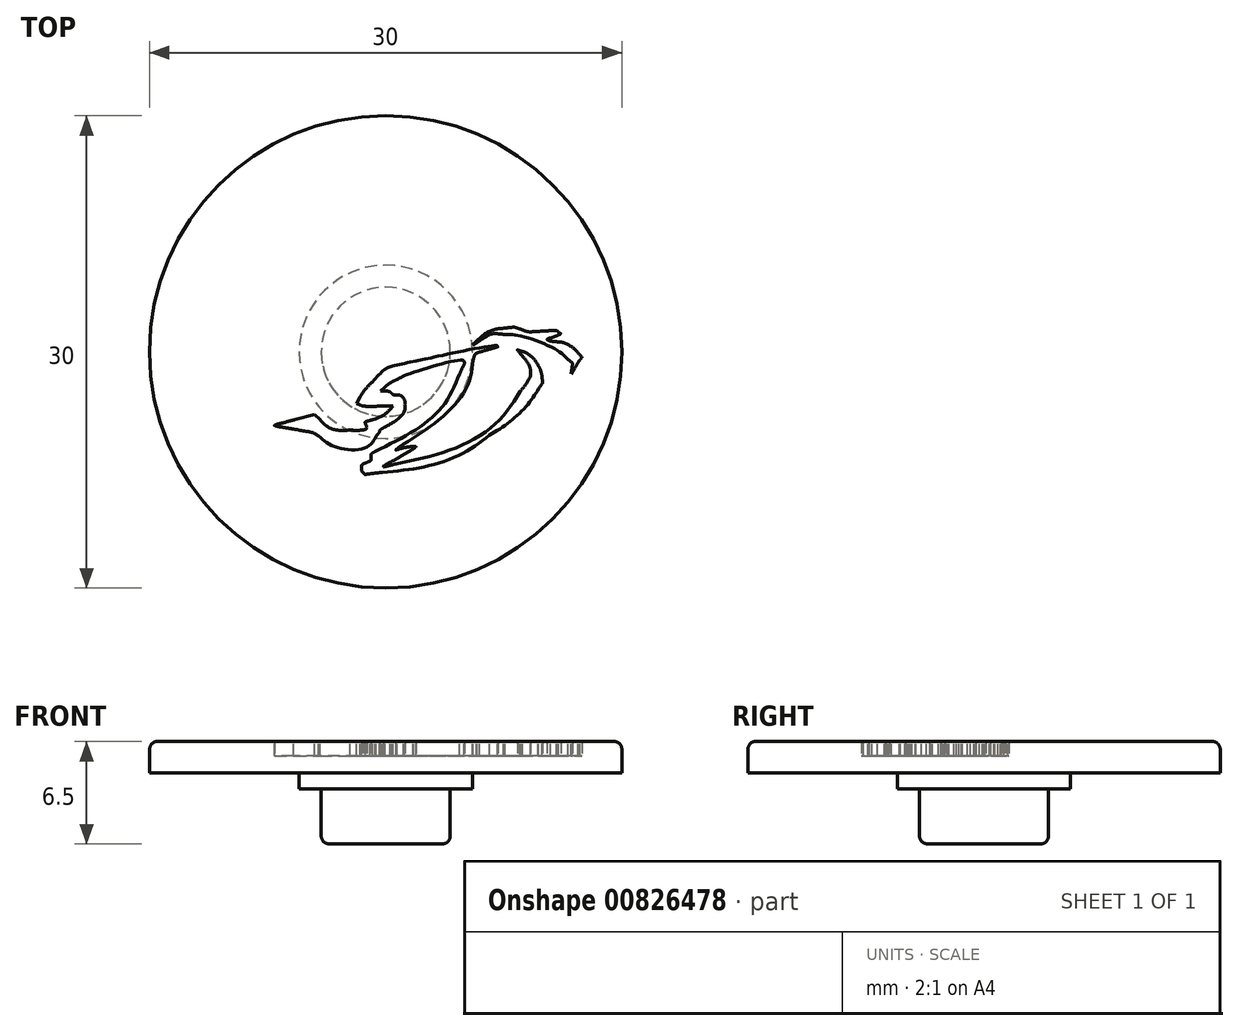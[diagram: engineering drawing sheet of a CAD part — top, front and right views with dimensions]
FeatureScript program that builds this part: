
annotation { "Feature Type Name" : "Feature", "Feature Type Description" : "" }
export const myFeature = defineFeature(function(context is Context, id is Id, definition is map)
    precondition{}
    {
        {
            var Q0;
            Q0=qCreatedBy(makeId("Top.planeOp"),FACE);
            var sketch = newSketch(context, id + "F0", { "sketchPlane" : qUnion([Q0])});
            skFitSpline(sketch, "E0", {"points": [v(-1.44, -7.67) * mm, v(-1.49, -7.62) * mm, v(-1.53, -7.5) * mm, v(-1.53, -7.38) * mm]});
            skFitSpline(sketch, "E1", {"points": [v(-1.53, -7.38) * mm, v(-1.53, -7.2) * mm, v(-1.47, -7.14) * mm, v(-1.23, -7.03) * mm]});
            skFitSpline(sketch, "E2", {"points": [v(-1.23, -7.03) * mm, v(-0.97, -6.92) * mm, v(-0.92, -6.86) * mm, v(-0.92, -6.68) * mm]});
            skFitSpline(sketch, "E3", {"points": [v(-0.92, -6.68) * mm, v(-0.92, -6.52) * mm, v(-0.87, -6.44) * mm, v(-0.68, -6.34) * mm]});
            skFitSpline(sketch, "E4", {"points": [v(-0.68, -6.34) * mm, v(2.05, -4.85) * mm, v(3.75, -3.29) * mm, v(4.68, -1.4) * mm]});
            skFitSpline(sketch, "E5", {"points": [v(4.68, -1.4) * mm, v(4.88, -1.01) * mm, v(5.01, -0.68) * mm, v(4.99, -0.65) * mm]});
            skFitSpline(sketch, "E6", {"points": [v(4.99, -0.65) * mm, v(4.87, -0.53) * mm, v(1.46, -1.41) * mm, v(0.72, -1.76) * mm]});
            skFitSpline(sketch, "E7", {"points": [v(0.72, -1.76) * mm, v(0.46, -1.87) * mm, v(0.12, -2.09) * mm, v(-0.04, -2.23) * mm]});
            skFitSpline(sketch, "E8", {"points": [v(-0.06, -2.5) * mm, v(0.09, -2.5) * mm, v(0.27, -2.55) * mm, v(0.35, -2.62) * mm]});
            skFitSpline(sketch, "E9", {"points": [v(0.35, -2.62) * mm, v(0.43, -2.7) * mm, v(0.57, -2.75) * mm, v(0.66, -2.75) * mm]});
            skFitSpline(sketch, "E10", {"points": [v(0.66, -2.75) * mm, v(0.9, -2.75) * mm, v(1.2, -3.08) * mm, v(1.2, -3.34) * mm]});
            skFitSpline(sketch, "E11", {"points": [v(1.2, -3.34) * mm, v(1.2, -3.73) * mm, v(0.66, -4.35) * mm, v(-0.06, -4.77) * mm]});
            skFitSpline(sketch, "E12", {"points": [v(-0.06, -4.77) * mm, v(-0.24, -4.88) * mm, v(-0.4, -5) * mm, v(-0.4, -5.03) * mm]});
            skFitSpline(sketch, "E13", {"points": [v(-0.4, -5.03) * mm, v(-0.4, -5.07) * mm, v(-0.5, -5.22) * mm, v(-0.62, -5.36) * mm]});
            skFitSpline(sketch, "E14", {"points": [v(-0.62, -5.36) * mm, v(-1.25, -6.07) * mm, v(-3.14, -6.06) * mm, v(-4.28, -5.34) * mm]});
            skFitSpline(sketch, "E15", {"points": [v(-4.28, -5.34) * mm, v(-4.56, -5.16) * mm, v(-4.85, -5.08) * mm, v(-5.85, -4.91) * mm]});
            skFitSpline(sketch, "E16", {"points": [v(-5.85, -4.91) * mm, v(-6.53, -4.8) * mm, v(-7.06, -4.68) * mm, v(-7.05, -4.67) * mm]});
            skFitSpline(sketch, "E17", {"points": [v(-7.05, -4.67) * mm, v(-7.03, -4.65) * mm, v(-6.46, -4.5) * mm, v(-5.77, -4.31) * mm]});
            skLineSegment(sketch, "E18", {"start": v(-0.04, -2.23) * mm, "end": v(-0.34, -2.5) * mm});
            skLineSegment(sketch, "E19", {"start": v(-0.34, -2.5) * mm, "end": v(-0.06, -2.5) * mm});
            skFitSpline(sketch, "E20", {"points": [v(-4.17, -4.31) * mm, v(-3.65, -4.78) * mm, v(-3.1, -4.97) * mm, v(-2.27, -4.97) * mm]});
            skFitSpline(sketch, "E21", {"points": [v(-2.27, -4.97) * mm, v(-1.54, -4.97) * mm, v(-1.2, -4.85) * mm, v(-1.28, -4.59) * mm]});
            skFitSpline(sketch, "E22", {"points": [v(-1.28, -4.59) * mm, v(-1.3, -4.48) * mm, v(-1.25, -4.43) * mm, v(-0.98, -4.35) * mm]});
            skFitSpline(sketch, "E23", {"points": [v(-0.98, -4.35) * mm, v(-0.53, -4.22) * mm, v(0.01, -3.91) * mm, v(0.26, -3.66) * mm]});
            skLineSegment(sketch, "E24", {"start": v(-5.77, -4.31) * mm, "end": v(-4.53, -3.99) * mm});
            skLineSegment(sketch, "E25", {"start": v(-4.53, -3.99) * mm, "end": v(-4.17, -4.31) * mm});
            skFitSpline(sketch, "E26", {"points": [v(-0.48, -3.46) * mm, v(-1.07, -3.46) * mm, v(-1.5, -3.43) * mm, v(-1.63, -3.37) * mm]});
            skLineSegment(sketch, "E27", {"start": v(0.26, -3.66) * mm, "end": v(0.46, -3.44) * mm});
            skLineSegment(sketch, "E28", {"start": v(0.46, -3.44) * mm, "end": v(-0.48, -3.46) * mm});
            skFitSpline(sketch, "E29", {"points": [v(-1.63, -2.88) * mm, v(-1.51, -2.66) * mm, v(-1.16, -2.22) * mm, v(-0.85, -1.9) * mm]});
            skFitSpline(sketch, "E30", {"points": [v(-0.85, -1.9) * mm, v(-0.09, -1.14) * mm, v(0.37, -0.92) * mm, v(1.93, -0.58) * mm]});
            skFitSpline(sketch, "E31", {"points": [v(1.93, -0.58) * mm, v(3.42, -0.26) * mm, v(7.06, 0.4) * mm, v(7.1, 0.35) * mm]});
            skFitSpline(sketch, "E32", {"points": [v(7.1, 0.35) * mm, v(7.12, 0.33) * mm, v(6.86, 0.23) * mm, v(6.5, 0.14) * mm]});
            skFitSpline(sketch, "E33", {"points": [v(6.5, 0.14) * mm, v(6.16, 0.04) * mm, v(5.83, -0.06) * mm, v(5.76, -0.1) * mm]});
            skFitSpline(sketch, "E34", {"points": [v(5.76, -0.1) * mm, v(5.7, -0.13) * mm, v(5.6, -0.34) * mm, v(5.55, -0.56) * mm]});
            skFitSpline(sketch, "E35", {"points": [v(5.55, -0.56) * mm, v(5.17, -2.2) * mm, v(3.48, -4.23) * mm, v(1.13, -5.87) * mm]});
            skFitSpline(sketch, "E36", {"points": [v(1.13, -5.87) * mm, v(0.82, -6.08) * mm, v(0.63, -6.24) * mm, v(0.71, -6.22) * mm]});
            skFitSpline(sketch, "E37", {"points": [v(0.71, -6.22) * mm, v(1.08, -6.11) * mm, v(1.56, -6.02) * mm, v(1.74, -6.02) * mm]});
            skFitSpline(sketch, "E38", {"points": [v(1.74, -6.02) * mm, v(1.92, -6.02) * mm, v(1.92, -6.02) * mm, v(1.78, -6.14) * mm]});
            skFitSpline(sketch, "E39", {"points": [v(1.78, -6.14) * mm, v(1.7, -6.2) * mm, v(1.22, -6.48) * mm, v(0.73, -6.76) * mm]});
            skFitSpline(sketch, "E40", {"points": [v(0.73, -6.76) * mm, v(0.24, -7.04) * mm, v(-0.15, -7.27) * mm, v(-0.13, -7.29) * mm]});
            skFitSpline(sketch, "E41", {"points": [v(-0.13, -7.29) * mm, v(-0.12, -7.3) * mm, v(0.23, -7.22) * mm, v(0.64, -7.12) * mm]});
            skFitSpline(sketch, "E42", {"points": [v(0.64, -7.12) * mm, v(4.15, -6.21) * mm, v(6.96, -4.58) * mm, v(8.53, -2.53) * mm]});
            skFitSpline(sketch, "E43", {"points": [v(8.53, -2.53) * mm, v(8.88, -2.08) * mm, v(9.19, -1.53) * mm, v(9.19, -1.36) * mm]});
            skFitSpline(sketch, "E44", {"points": [v(9.19, -1.36) * mm, v(9.19, -1.08) * mm, v(8.99, -0.65) * mm, v(8.7, -0.28) * mm]});
            skFitSpline(sketch, "E45", {"points": [v(8.7, -0.28) * mm, v(8.38, 0.1) * mm, v(8.37, 0.12) * mm, v(8.56, 0.06) * mm]});
            skFitSpline(sketch, "E46", {"points": [v(8.56, 0.06) * mm, v(8.93, -0.08) * mm, v(9.48, -0.53) * mm, v(9.68, -0.88) * mm]});
            skFitSpline(sketch, "E47", {"points": [v(9.68, -0.88) * mm, v(9.79, -1.06) * mm, v(9.9, -1.38) * mm, v(9.92, -1.6) * mm]});
            skFitSpline(sketch, "E48", {"points": [v(9.92, -1.6) * mm, v(9.96, -1.93) * mm, v(9.94, -2) * mm, v(9.72, -2.33) * mm]});
            skFitSpline(sketch, "E49", {"points": [v(9.72, -2.33) * mm, v(9.03, -3.34) * mm, v(7.85, -4.46) * mm, v(6.6, -5.3) * mm]});
            skFitSpline(sketch, "E50", {"points": [v(6.6, -5.3) * mm, v(4.85, -6.47) * mm, v(2.43, -7.3) * mm, v(-0.2, -7.65) * mm]});
            skFitSpline(sketch, "E51", {"points": [v(-0.2, -7.65) * mm, v(-1.29, -7.79) * mm, v(-1.32, -7.8) * mm, v(-1.44, -7.67) * mm]});
            skLineSegment(sketch, "E52", {"start": v(-1.63, -3.37) * mm, "end": v(-1.84, -3.28) * mm});
            skLineSegment(sketch, "E53", {"start": v(-1.84, -3.28) * mm, "end": v(-1.63, -2.88) * mm});
            skFitSpline(sketch, "E54", {"points": [v(-7.59, -3.23) * mm, v(-7.06, -2.2) * mm, v(-7.01, -1.09) * mm, v(-7.46, -0.25) * mm]});
            skFitSpline(sketch, "E55", {"points": [v(-7.46, -0.25) * mm, v(-8.22, 1.18) * mm, v(-9.95, 2.18) * mm, v(-13.43, 3.2) * mm]});
            skFitSpline(sketch, "E56", {"points": [v(-13.43, 3.2) * mm, v(-13.8, 3.31) * mm, v(-13.74, 3.32) * mm, v(-12.25, 3.32) * mm]});
            skFitSpline(sketch, "E57", {"points": [v(-12.25, 3.32) * mm, v(-10.97, 3.32) * mm, v(-10.56, 3.35) * mm, v(-9.94, 3.48) * mm]});
            skFitSpline(sketch, "E58", {"points": [v(-9.94, 3.48) * mm, v(-8.94, 3.69) * mm, v(-8.97, 3.7) * mm, v(-9.13, 3.35) * mm]});
            skFitSpline(sketch, "E59", {"points": [v(-9.13, 3.35) * mm, v(-9.4, 2.79) * mm, v(-9.4, 2.77) * mm, v(-8.95, 2.55) * mm]});
            skLineSegment(sketch, "E60", {"start": v(-1.44, -7.67) * mm, "end": v(-1.44, -7.67) * mm});
            skFitSpline(sketch, "E61", {"points": [v(-8.2, 2.8) * mm, v(-7.9, 3.18) * mm, v(-7.03, 3.86) * mm, v(-6.84, 3.86) * mm]});
            skFitSpline(sketch, "E62", {"points": [v(-6.84, 3.86) * mm, v(-6.72, 3.86) * mm, v(-6.78, 3.7) * mm, v(-7, 3.4) * mm]});
            skFitSpline(sketch, "E63", {"points": [v(-7, 3.4) * mm, v(-7.22, 3.13) * mm, v(-7.63, 2.32) * mm, v(-7.71, 2) * mm]});
            skFitSpline(sketch, "E64", {"points": [v(-7.71, 2) * mm, v(-7.74, 1.89) * mm, v(-7.66, 1.77) * mm, v(-7.36, 1.54) * mm]});
            skLineSegment(sketch, "E65", {"start": v(-8.95, 2.55) * mm, "end": v(-8.54, 2.35) * mm});
            skLineSegment(sketch, "E66", {"start": v(-8.54, 2.35) * mm, "end": v(-8.2, 2.8) * mm});
            skFitSpline(sketch, "E67", {"points": [v(-6.78, 1.63) * mm, v(-6.69, 1.86) * mm, v(-6.48, 2.2) * mm, v(-6.34, 2.38) * mm]});
            skFitSpline(sketch, "E68", {"points": [v(-6.34, 2.38) * mm, v(-6.08, 2.71) * mm, v(-5.24, 3.4) * mm, v(-5.1, 3.4) * mm]});
            skFitSpline(sketch, "E69", {"points": [v(-5.1, 3.4) * mm, v(-4.95, 3.4) * mm, v(-5.04, 3.16) * mm, v(-5.35, 2.7) * mm]});
            skFitSpline(sketch, "E70", {"points": [v(-5.35, 2.7) * mm, v(-5.83, 2) * mm, v(-6.01, 1.37) * mm, v(-6.1, 0.1) * mm]});
            skFitSpline(sketch, "E71", {"points": [v(-6.1, 0.1) * mm, v(-6.17, -1.02) * mm, v(-6.3, -1.64) * mm, v(-6.56, -2.16) * mm]});
            skFitSpline(sketch, "E72", {"points": [v(-6.56, -2.16) * mm, v(-6.79, -2.62) * mm, v(-7.26, -3.24) * mm, v(-7.54, -3.44) * mm]});
            skLineSegment(sketch, "E73", {"start": v(-7.36, 1.54) * mm, "end": v(-6.96, 1.23) * mm});
            skLineSegment(sketch, "E74", {"start": v(-6.96, 1.23) * mm, "end": v(-6.78, 1.63) * mm});
            skFitSpline(sketch, "E75", {"points": [v(-4.41, -2.77) * mm, v(-4.42, -2.13) * mm, v(-4.2, -1.56) * mm, v(-3.73, -1.05) * mm]});
            skFitSpline(sketch, "E76", {"points": [v(-3.73, -1.05) * mm, v(-3.53, -0.83) * mm, v(-3.2, -0.56) * mm, v(-3.01, -0.46) * mm]});
            skFitSpline(sketch, "E77", {"points": [v(-3.01, -0.46) * mm, v(-2.71, -0.3) * mm, v(-2.65, -0.23) * mm, v(-2.55, 0.1) * mm]});
            skFitSpline(sketch, "E78", {"points": [v(-2.55, 0.1) * mm, v(-2.43, 0.52) * mm, v(-2.41, 0.89) * mm, v(-2.51, 1.04) * mm]});
            skFitSpline(sketch, "E79", {"points": [v(-2.51, 1.04) * mm, v(-2.61, 1.2) * mm, v(-3.05, 1.11) * mm, v(-3.83, 0.79) * mm]});
            skFitSpline(sketch, "E80", {"points": [v(-3.83, 0.79) * mm, v(-5.04, 0.27) * mm, v(-5.33, -0.03) * mm, v(-5.33, -0.8) * mm]});
            skFitSpline(sketch, "E81", {"points": [v(-5.33, -0.8) * mm, v(-5.33, -1.06) * mm, v(-5.3, -1.4) * mm, v(-5.26, -1.55) * mm]});
            skFitSpline(sketch, "E82", {"points": [v(-5.26, -1.55) * mm, v(-5.23, -1.7) * mm, v(-5.22, -1.82) * mm, v(-5.25, -1.8) * mm]});
            skFitSpline(sketch, "E83", {"points": [v(-5.25, -1.8) * mm, v(-5.38, -1.72) * mm, v(-5.5, -0.74) * mm, v(-5.46, -0.1) * mm]});
            skFitSpline(sketch, "E84", {"points": [v(-5.46, -0.1) * mm, v(-5.42, 0.63) * mm, v(-5.22, 1.25) * mm, v(-4.84, 1.83) * mm]});
            skLineSegment(sketch, "E85", {"start": v(-7.54, -3.44) * mm, "end": v(-7.78, -3.6) * mm});
            skLineSegment(sketch, "E86", {"start": v(-7.78, -3.6) * mm, "end": v(-7.59, -3.23) * mm});
            skFitSpline(sketch, "E87", {"points": [v(-2.15, 2.2) * mm, v(0.25, 2.2) * mm, v(0.32, 2.2) * mm, v(0.59, 2.36) * mm]});
            skFitSpline(sketch, "E88", {"points": [v(0.59, 2.36) * mm, v(1.61, 2.98) * mm, v(2.34, 3.8) * mm, v(2.5, 4.5) * mm]});
            skFitSpline(sketch, "E89", {"points": [v(2.5, 4.5) * mm, v(2.59, 4.88) * mm, v(2.52, 5.38) * mm, v(2.32, 5.85) * mm]});
            skFitSpline(sketch, "E90", {"points": [v(2.32, 5.85) * mm, v(2.27, 5.95) * mm, v(2.37, 5.98) * mm, v(3.05, 6.02) * mm]});
            skFitSpline(sketch, "E91", {"points": [v(3.05, 6.02) * mm, v(3.48, 6.05) * mm, v(4, 6.1) * mm, v(4.2, 6.11) * mm]});
            skLineSegment(sketch, "E92", {"start": v(-4.84, 1.83) * mm, "end": v(-4.6, 2.19) * mm});
            skLineSegment(sketch, "E93", {"start": v(-4.6, 2.19) * mm, "end": v(-2.15, 2.2) * mm});
            skFitSpline(sketch, "E94", {"points": [v(4.36, 6.03) * mm, v(4.02, 5.84) * mm, v(3.57, 5.38) * mm, v(3.39, 5.04) * mm]});
            skFitSpline(sketch, "E95", {"points": [v(3.39, 5.04) * mm, v(3.25, 4.8) * mm, v(3.22, 4.61) * mm, v(3.22, 4.05) * mm]});
            skFitSpline(sketch, "E96", {"points": [v(3.22, 4.05) * mm, v(3.22, 3.33) * mm, v(3.29, 3.13) * mm, v(3.69, 2.6) * mm]});
            skLineSegment(sketch, "E97", {"start": v(4.2, 6.11) * mm, "end": v(4.59, 6.15) * mm});
            skLineSegment(sketch, "E98", {"start": v(4.59, 6.15) * mm, "end": v(4.36, 6.03) * mm});
            skFitSpline(sketch, "E99", {"points": [v(9.16, 2.14) * mm, v(9.58, 1.94) * mm, v(10.16, 1.87) * mm, v(10.58, 1.99) * mm]});
            skLineSegment(sketch, "E100", {"start": v(3.69, 2.6) * mm, "end": v(3.87, 2.34) * mm});
            skLineSegment(sketch, "E101", {"start": v(3.87, 2.34) * mm, "end": v(6.31, 2.34) * mm});
            skLineSegment(sketch, "E102", {"start": v(6.31, 2.34) * mm, "end": v(8.75, 2.34) * mm});
            skLineSegment(sketch, "E103", {"start": v(8.75, 2.34) * mm, "end": v(9.16, 2.14) * mm});
            skFitSpline(sketch, "E104", {"points": [v(10.27, 2.6) * mm, v(9.76, 3.16) * mm, v(9.5, 3.57) * mm, v(9.5, 3.82) * mm]});
            skFitSpline(sketch, "E105", {"points": [v(9.5, 3.82) * mm, v(9.5, 4.05) * mm, v(9.1, 4.82) * mm, v(8.78, 5.2) * mm]});
            skLineSegment(sketch, "E106", {"start": v(10.58, 1.99) * mm, "end": v(10.8, 2.05) * mm});
            skLineSegment(sketch, "E107", {"start": v(10.8, 2.05) * mm, "end": v(10.27, 2.6) * mm});
            skFitSpline(sketch, "E108", {"points": [v(8.92, 5.32) * mm, v(9.92, 4.76) * mm, v(9.97, 4.71) * mm, v(10.08, 4.17) * mm]});
            skFitSpline(sketch, "E109", {"points": [v(10.08, 4.17) * mm, v(10.19, 3.63) * mm, v(10.24, 3.53) * mm, v(10.7, 3.01) * mm]});
            skFitSpline(sketch, "E110", {"points": [v(10.7, 3.01) * mm, v(10.94, 2.75) * mm, v(11.24, 2.54) * mm, v(11.9, 2.2) * mm]});
            skLineSegment(sketch, "E111", {"start": v(8.78, 5.2) * mm, "end": v(8.46, 5.57) * mm});
            skLineSegment(sketch, "E112", {"start": v(8.46, 5.57) * mm, "end": v(8.92, 5.32) * mm});
            skFitSpline(sketch, "E113", {"points": [v(13.22, -0.8) * mm, v(13, -1.09) * mm, v(12.77, -1.45) * mm, v(12.69, -1.6) * mm]});
            skFitSpline(sketch, "E114", {"points": [v(12.69, -1.6) * mm, v(12.5, -1.97) * mm, v(12.45, -2) * mm, v(11.77, -2.25) * mm]});
            skLineSegment(sketch, "E115", {"start": v(11.9, 2.2) * mm, "end": v(12.8, 1.75) * mm});
            skLineSegment(sketch, "E116", {"start": v(12.8, 1.75) * mm, "end": v(13.2, 0.73) * mm});
            skLineSegment(sketch, "E117", {"start": v(13.2, 0.73) * mm, "end": v(13.62, -0.3) * mm});
            skLineSegment(sketch, "E118", {"start": v(13.62, -0.3) * mm, "end": v(13.22, -0.8) * mm});
            skFitSpline(sketch, "E119", {"points": [v(11.74, -1.9) * mm, v(12.07, -1.56) * mm, v(12.4, -1.14) * mm, v(12.56, -0.82) * mm]});
            skLineSegment(sketch, "E120", {"start": v(11.77, -2.25) * mm, "end": v(11.2, -2.45) * mm});
            skLineSegment(sketch, "E121", {"start": v(11.2, -2.45) * mm, "end": v(11.74, -1.9) * mm});
            skFitSpline(sketch, "E122", {"points": [v(12.53, 0.11) * mm, v(12.36, 0.33) * mm, v(12.1, 0.6) * mm, v(11.96, 0.73) * mm]});
            skFitSpline(sketch, "E123", {"points": [v(11.96, 0.73) * mm, v(11.66, 0.97) * mm, v(11.63, 1.05) * mm, v(11.85, 1.05) * mm]});
            skFitSpline(sketch, "E124", {"points": [v(11.85, 1.05) * mm, v(12.05, 1.05) * mm, v(12.3, 1.18) * mm, v(12.3, 1.29) * mm]});
            skFitSpline(sketch, "E125", {"points": [v(12.3, 1.29) * mm, v(12.3, 1.33) * mm, v(12.01, 1.5) * mm, v(11.66, 1.66) * mm]});
            skLineSegment(sketch, "E126", {"start": v(12.56, -0.82) * mm, "end": v(12.83, -0.29) * mm});
            skLineSegment(sketch, "E127", {"start": v(12.83, -0.29) * mm, "end": v(12.53, 0.11) * mm});
            skFitSpline(sketch, "E128", {"points": [v(10.67, 1.8) * mm, v(10.15, 1.58) * mm, v(9.34, 1.53) * mm, v(8.73, 1.7) * mm]});
            skFitSpline(sketch, "E129", {"points": [v(8.73, 1.7) * mm, v(7.8, 1.96) * mm, v(6.77, 1.78) * mm, v(5.94, 1.24) * mm]});
            skLineSegment(sketch, "E130", {"start": v(11.66, 1.66) * mm, "end": v(11.02, 1.96) * mm});
            skLineSegment(sketch, "E131", {"start": v(11.02, 1.96) * mm, "end": v(10.67, 1.8) * mm});
            skFitSpline(sketch, "E132", {"points": [v(5.54, 1.24) * mm, v(5.54, 1.59) * mm, v(5.38, 1.65) * mm, v(4.5, 1.67) * mm]});
            skFitSpline(sketch, "E133", {"points": [v(4.5, 1.67) * mm, v(3.68, 1.67) * mm, v(3.51, 1.61) * mm, v(3, 1.12) * mm]});
            skLineSegment(sketch, "E134", {"start": v(5.94, 1.24) * mm, "end": v(5.54, 0.97) * mm});
            skLineSegment(sketch, "E135", {"start": v(5.54, 0.97) * mm, "end": v(5.54, 1.24) * mm});
            skFitSpline(sketch, "E136", {"points": [v(2.24, 0.83) * mm, v(1.9, 0.91) * mm, v(1.89, 0.93) * mm, v(1.89, 1.2) * mm]});
            skFitSpline(sketch, "E137", {"points": [v(1.89, 1.2) * mm, v(1.89, 1.35) * mm, v(1.92, 1.6) * mm, v(1.96, 1.74) * mm]});
            skLineSegment(sketch, "E138", {"start": v(3, 1.12) * mm, "end": v(2.6, 0.74) * mm});
            skLineSegment(sketch, "E139", {"start": v(2.6, 0.74) * mm, "end": v(2.24, 0.83) * mm});
            skFitSpline(sketch, "E140", {"points": [v(1.85, 1.8) * mm, v(1.75, 1.68) * mm, v(1.6, 1.41) * mm, v(1.54, 1.2) * mm]});
            skFitSpline(sketch, "E141", {"points": [v(1.54, 1.2) * mm, v(1.42, 0.87) * mm, v(1.38, 0.83) * mm, v(1.13, 0.8) * mm]});
            skFitSpline(sketch, "E142", {"points": [v(1.13, 0.8) * mm, v(0.99, 0.78) * mm, v(0.85, 0.78) * mm, v(0.83, 0.8) * mm]});
            skFitSpline(sketch, "E143", {"points": [v(0.83, 0.8) * mm, v(0.8, 0.82) * mm, v(0.77, 1.03) * mm, v(0.75, 1.27) * mm]});
            skLineSegment(sketch, "E144", {"start": v(1.96, 1.74) * mm, "end": v(2.04, 2) * mm});
            skLineSegment(sketch, "E145", {"start": v(2.04, 2) * mm, "end": v(1.85, 1.8) * mm});
            skFitSpline(sketch, "E146", {"points": [v(0.58, 1.4) * mm, v(0.5, 1.24) * mm, v(0.45, 1.01) * mm, v(0.45, 0.9) * mm]});
            skFitSpline(sketch, "E147", {"points": [v(0.45, 0.9) * mm, v(0.45, 0.76) * mm, v(0.38, 0.65) * mm, v(0.25, 0.56) * mm]});
            skFitSpline(sketch, "E148", {"points": [v(0.25, 0.56) * mm, v(0.02, 0.4) * mm, v(0.03, 0.4) * mm, v(-0.21, 0.88) * mm]});
            skLineSegment(sketch, "E149", {"start": v(0.75, 1.27) * mm, "end": v(0.7, 1.7) * mm});
            skLineSegment(sketch, "E150", {"start": v(0.7, 1.7) * mm, "end": v(0.58, 1.4) * mm});
            skFitSpline(sketch, "E151", {"points": [v(-0.38, 0.75) * mm, v(-0.36, 0.25) * mm, v(-0.48, -0.09) * mm, v(-0.66, -0.09) * mm]});
            skFitSpline(sketch, "E152", {"points": [v(-0.66, -0.09) * mm, v(-0.7, -0.09) * mm, v(-0.87, 0.03) * mm, v(-1.03, 0.18) * mm]});
            skLineSegment(sketch, "E153", {"start": v(-0.21, 0.88) * mm, "end": v(-0.4, 1.24) * mm});
            skLineSegment(sketch, "E154", {"start": v(-0.4, 1.24) * mm, "end": v(-0.38, 0.75) * mm});
            skFitSpline(sketch, "E155", {"points": [v(-1.26, 0.24) * mm, v(-1.23, 0.12) * mm, v(-1.16, -0.07) * mm, v(-1.1, -0.2) * mm]});
            skFitSpline(sketch, "E156", {"points": [v(-1.1, -0.2) * mm, v(-1.05, -0.31) * mm, v(-1.02, -0.49) * mm, v(-1.04, -0.58) * mm]});
            skFitSpline(sketch, "E157", {"points": [v(-1.04, -0.58) * mm, v(-1.08, -0.74) * mm, v(-1.14, -0.76) * mm, v(-1.78, -0.79) * mm]});
            skFitSpline(sketch, "E158", {"points": [v(-1.78, -0.79) * mm, v(-2.34, -0.81) * mm, v(-2.56, -0.86) * mm, v(-2.86, -1.02) * mm]});
            skFitSpline(sketch, "E159", {"points": [v(-2.86, -1.02) * mm, v(-3.57, -1.39) * mm, v(-4.2, -2.2) * mm, v(-4.34, -2.93) * mm]});
            skFitSpline(sketch, "E160", {"points": [v(-4.34, -2.93) * mm, v(-4.4, -3.24) * mm, v(-4.4, -3.23) * mm, v(-4.41, -2.77) * mm]});
            skLineSegment(sketch, "E161", {"start": v(-1.03, 0.18) * mm, "end": v(-1.3, 0.46) * mm});
            skLineSegment(sketch, "E162", {"start": v(-1.3, 0.46) * mm, "end": v(-1.26, 0.24) * mm});
            skFitSpline(sketch, "E163", {"points": [v(11.82, -1.07) * mm, v(11.86, -0.74) * mm, v(11.85, -0.71) * mm, v(11.57, -0.48) * mm]});
            skFitSpline(sketch, "E164", {"points": [v(11.57, -0.48) * mm, v(10.86, 0.11) * mm, v(8.5, 1.03) * mm, v(7.48, 1.1) * mm]});
            skFitSpline(sketch, "E165", {"points": [v(7.48, 1.1) * mm, v(6.85, 1.15) * mm, v(6.59, 1.09) * mm, v(5.95, 0.7) * mm]});
            skFitSpline(sketch, "E166", {"points": [v(5.8, 0.7) * mm, v(6.28, 1.13) * mm, v(6.94, 1.42) * mm, v(7.59, 1.5) * mm]});
            skFitSpline(sketch, "E167", {"points": [v(7.59, 1.5) * mm, v(8.08, 1.56) * mm, v(8.22, 1.55) * mm, v(8.62, 1.42) * mm]});
            skFitSpline(sketch, "E168", {"points": [v(8.62, 1.42) * mm, v(9.02, 1.28) * mm, v(9.18, 1.27) * mm, v(9.95, 1.31) * mm]});
            skFitSpline(sketch, "E169", {"points": [v(9.95, 1.31) * mm, v(10.66, 1.36) * mm, v(10.85, 1.34) * mm, v(10.97, 1.25) * mm]});
            skFitSpline(sketch, "E170", {"points": [v(10.97, 1.25) * mm, v(11.12, 1.14) * mm, v(11.12, 1.14) * mm, v(10.9, 1.05) * mm]});
            skFitSpline(sketch, "E171", {"points": [v(10.9, 1.05) * mm, v(10.77, 1) * mm, v(10.58, 0.93) * mm, v(10.48, 0.89) * mm]});
            skFitSpline(sketch, "E172", {"points": [v(10.48, 0.89) * mm, v(10.24, 0.8) * mm, v(10.36, 0.72) * mm, v(10.85, 0.64) * mm]});
            skFitSpline(sketch, "E173", {"points": [v(10.85, 0.64) * mm, v(11.3, 0.57) * mm, v(11.9, 0.25) * mm, v(12.21, -0.07) * mm]});
            skFitSpline(sketch, "E174", {"points": [v(12.21, -0.07) * mm, v(12.45, -0.32) * mm, v(12.46, -0.34) * mm, v(12.34, -0.5) * mm]});
            skFitSpline(sketch, "E175", {"points": [v(12.34, -0.5) * mm, v(12.28, -0.59) * mm, v(12.12, -0.83) * mm, v(12, -1.04) * mm]});
            skLineSegment(sketch, "E176", {"start": v(5.95, 0.7) * mm, "end": v(5.5, 0.44) * mm});
            skLineSegment(sketch, "E177", {"start": v(5.5, 0.44) * mm, "end": v(5.8, 0.7) * mm});
            skFitSpline(sketch, "E178", {"points": [v(-1.45, 2.92) * mm, v(-1.45, 2.94) * mm, v(-1.4, 3.08) * mm, v(-1.34, 3.22) * mm]});
            skLineSegment(sketch, "E179", {"start": v(12, -1.04) * mm, "end": v(11.77, -1.42) * mm});
            skLineSegment(sketch, "E180", {"start": v(11.77, -1.42) * mm, "end": v(11.82, -1.07) * mm});
            skFitSpline(sketch, "E181", {"points": [v(-1.61, 3.65) * mm, v(-1.94, 3.78) * mm, v(-2.5, 4.28) * mm, v(-2.43, 4.36) * mm]});
            skFitSpline(sketch, "E182", {"points": [v(-2.43, 4.36) * mm, v(-2.41, 4.38) * mm, v(-2.21, 4.3) * mm, v(-1.98, 4.2) * mm]});
            skFitSpline(sketch, "E183", {"points": [v(-1.98, 4.2) * mm, v(-1.7, 4.05) * mm, v(-1.4, 3.98) * mm, v(-1.03, 3.96) * mm]});
            skLineSegment(sketch, "E184", {"start": v(-1.34, 3.22) * mm, "end": v(-1.23, 3.48) * mm});
            skLineSegment(sketch, "E185", {"start": v(-1.23, 3.48) * mm, "end": v(-1.61, 3.65) * mm});
            skFitSpline(sketch, "E186", {"points": [v(0.02, 4.5) * mm, v(0.5, 5.03) * mm, v(0.55, 5.07) * mm, v(0.92, 5.12) * mm]});
            skFitSpline(sketch, "E187", {"points": [v(0.92, 5.12) * mm, v(1.62, 5.22) * mm, v(1.65, 5.26) * mm, v(1.22, 5.45) * mm]});
            skFitSpline(sketch, "E188", {"points": [v(1.22, 5.45) * mm, v(0.47, 5.77) * mm, v(0.47, 5.77) * mm, v(-0.08, 5.08) * mm]});
            skFitSpline(sketch, "E189", {"points": [v(-0.08, 5.08) * mm, v(-0.35, 4.75) * mm, v(-0.58, 4.48) * mm, v(-0.6, 4.5) * mm]});
            skFitSpline(sketch, "E190", {"points": [v(-0.6, 4.5) * mm, v(-0.6, 4.51) * mm, v(-0.52, 4.82) * mm, v(-0.4, 5.18) * mm]});
            skFitSpline(sketch, "E191", {"points": [v(-0.4, 5.18) * mm, v(-0.27, 5.55) * mm, v(-0.2, 5.86) * mm, v(-0.24, 5.88) * mm]});
            skFitSpline(sketch, "E192", {"points": [v(-0.24, 5.88) * mm, v(-0.3, 5.92) * mm, v(-1.15, 5.08) * mm, v(-1.21, 4.92) * mm]});
            skFitSpline(sketch, "E193", {"points": [v(-1.21, 4.92) * mm, v(-1.23, 4.88) * mm, v(-1.27, 4.85) * mm, v(-1.3, 4.85) * mm]});
            skFitSpline(sketch, "E194", {"points": [v(-1.3, 4.85) * mm, v(-1.34, 4.85) * mm, v(-1.27, 5.08) * mm, v(-1.15, 5.35) * mm]});
            skFitSpline(sketch, "E195", {"points": [v(-1.15, 5.35) * mm, v(-0.88, 5.96) * mm, v(-0.87, 6) * mm, v(-1.1, 6) * mm]});
            skFitSpline(sketch, "E196", {"points": [v(-1.1, 6) * mm, v(-1.24, 6) * mm, v(-1.4, 5.88) * mm, v(-1.61, 5.61) * mm]});
            skFitSpline(sketch, "E197", {"points": [v(-1.61, 5.61) * mm, v(-1.8, 5.4) * mm, v(-1.95, 5.25) * mm, v(-1.97, 5.26) * mm]});
            skFitSpline(sketch, "E198", {"points": [v(-1.97, 5.26) * mm, v(-1.98, 5.28) * mm, v(-1.96, 5.47) * mm, v(-1.93, 5.68) * mm]});
            skLineSegment(sketch, "E199", {"start": v(-1.03, 3.96) * mm, "end": v(-0.5, 3.92) * mm});
            skLineSegment(sketch, "E200", {"start": v(-0.5, 3.92) * mm, "end": v(0.02, 4.5) * mm});
            skFitSpline(sketch, "E201", {"points": [v(-2.5, 6.07) * mm, v(-3.05, 6.07) * mm, v(-3.13, 6.05) * mm, v(-3.06, 5.96) * mm]});
            skFitSpline(sketch, "E202", {"points": [v(-3.06, 5.96) * mm, v(-2.99, 5.88) * mm, v(-2.99, 5.77) * mm, v(-3.05, 5.55) * mm]});
            skFitSpline(sketch, "E203", {"points": [v(-3.05, 5.55) * mm, v(-3.12, 5.28) * mm, v(-3.16, 5.25) * mm, v(-3.43, 5.2) * mm]});
            skFitSpline(sketch, "E204", {"points": [v(-3.43, 5.2) * mm, v(-3.67, 5.16) * mm, v(-3.9, 5.22) * mm, v(-4.58, 5.47) * mm]});
            skFitSpline(sketch, "E205", {"points": [v(-4.58, 5.47) * mm, v(-5.5, 5.82) * mm, v(-5.51, 5.84) * mm, v(-4.7, 6) * mm]});
            skFitSpline(sketch, "E206", {"points": [v(-4.7, 6) * mm, v(-4.32, 6.07) * mm, v(-4.27, 6.1) * mm, v(-4.27, 6.25) * mm]});
            skFitSpline(sketch, "E207", {"points": [v(-4.27, 6.25) * mm, v(-4.27, 6.35) * mm, v(-4.22, 6.47) * mm, v(-4.16, 6.52) * mm]});
            skFitSpline(sketch, "E208", {"points": [v(-4.16, 6.52) * mm, v(-4.02, 6.64) * mm, v(-2.37, 6.77) * mm, v(-1.8, 6.7) * mm]});
            skFitSpline(sketch, "E209", {"points": [v(-1.8, 6.7) * mm, v(-1.4, 6.67) * mm, v(-0.9, 6.75) * mm, v(1.4, 7.21) * mm]});
            skLineSegment(sketch, "E210", {"start": v(-1.93, 5.68) * mm, "end": v(-1.86, 6.07) * mm});
            skLineSegment(sketch, "E211", {"start": v(-1.86, 6.07) * mm, "end": v(-2.5, 6.07) * mm});
            skFitSpline(sketch, "E212", {"points": [v(5.13, 7.33) * mm, v(5.67, 7.09) * mm, v(6.13, 6.87) * mm, v(6.16, 6.84) * mm]});
            skFitSpline(sketch, "E213", {"points": [v(6.16, 6.84) * mm, v(6.2, 6.81) * mm, v(5.73, 6.81) * mm, v(5.14, 6.84) * mm]});
            skFitSpline(sketch, "E214", {"points": [v(5.14, 6.84) * mm, v(4.18, 6.89) * mm, v(3.96, 6.87) * mm, v(3.22, 6.71) * mm]});
            skFitSpline(sketch, "E215", {"points": [v(3.22, 6.71) * mm, v(1.46, 6.34) * mm, v(0.52, 6.11) * mm, v(0.58, 6.07) * mm]});
            skFitSpline(sketch, "E216", {"points": [v(0.58, 6.07) * mm, v(0.61, 6.04) * mm, v(0.88, 5.93) * mm, v(1.17, 5.81) * mm]});
            skFitSpline(sketch, "E217", {"points": [v(1.17, 5.81) * mm, v(1.46, 5.7) * mm, v(1.77, 5.56) * mm, v(1.85, 5.5) * mm]});
            skFitSpline(sketch, "E218", {"points": [v(1.85, 5.5) * mm, v(2.06, 5.34) * mm, v(2.1, 4.67) * mm, v(1.91, 4.32) * mm]});
            skFitSpline(sketch, "E219", {"points": [v(1.91, 4.32) * mm, v(1.79, 4.08) * mm, v(1.73, 4.05) * mm, v(1.36, 4) * mm]});
            skFitSpline(sketch, "E220", {"points": [v(1.36, 4) * mm, v(0.8, 3.92) * mm, v(0.1, 3.58) * mm, v(-0.3, 3.2) * mm]});
            skFitSpline(sketch, "E221", {"points": [v(-0.3, 3.2) * mm, v(-0.6, 2.9) * mm, v(-0.65, 2.88) * mm, v(-1.04, 2.88) * mm]});
            skFitSpline(sketch, "E222", {"points": [v(-1.04, 2.88) * mm, v(-1.27, 2.88) * mm, v(-1.45, 2.9) * mm, v(-1.45, 2.92) * mm]});
            skLineSegment(sketch, "E223", {"start": v(1.4, 7.21) * mm, "end": v(4.15, 7.76) * mm});
            skLineSegment(sketch, "E224", {"start": v(4.15, 7.76) * mm, "end": v(5.13, 7.33) * mm});
            skFitSpline(sketch, "E225", {"points": [v(7.74, 3.1) * mm, v(7.74, 3.22) * mm, v(7.7, 3.23) * mm, v(7.38, 3.2) * mm]});
            skFitSpline(sketch, "E226", {"points": [v(7.38, 3.2) * mm, v(7.07, 3.17) * mm, v(6.98, 3.2) * mm, v(6.77, 3.37) * mm]});
            skFitSpline(sketch, "E227", {"points": [v(6.77, 3.37) * mm, v(6.62, 3.5) * mm, v(6.5, 3.7) * mm, v(6.45, 3.89) * mm]});
            skFitSpline(sketch, "E228", {"points": [v(6.45, 3.89) * mm, v(6.38, 4.13) * mm, v(6.2, 4.36) * mm, v(5.74, 4.84) * mm]});
            skFitSpline(sketch, "E229", {"points": [v(5.74, 4.84) * mm, v(5.03, 5.57) * mm, v(5, 5.55) * mm, v(6.42, 5.11) * mm]});
            skFitSpline(sketch, "E230", {"points": [v(6.42, 5.11) * mm, v(7.71, 4.71) * mm, v(8.2, 4.32) * mm, v(8.2, 3.68) * mm]});
            skFitSpline(sketch, "E231", {"points": [v(8.2, 3.68) * mm, v(8.2, 3.3) * mm, v(8.7, 3.21) * mm, v(9, 3.53) * mm]});
            skFitSpline(sketch, "E232", {"points": [v(9, 3.53) * mm, v(9.21, 3.76) * mm, v(9.24, 3.72) * mm, v(9.07, 3.4) * mm]});
            skFitSpline(sketch, "E233", {"points": [v(9.07, 3.4) * mm, v(8.92, 3.1) * mm, v(8.6, 2.95) * mm, v(8.13, 2.95) * mm]});
            skFitSpline(sketch, "E234", {"points": [v(8.13, 2.95) * mm, v(7.8, 2.95) * mm, v(7.74, 2.97) * mm, v(7.74, 3.1) * mm]});
            skLineSegment(sketch, "E235", {"start": v(-1.45, 2.92) * mm, "end": v(-1.45, 2.92) * mm});
            skCircle(sketch, "E236", {"center": v(0, 0) * mm, "radius": 15 * mm});
            skSolve(sketch);
        }
        {
            var Q0;
            Q0=makeQuery(id+"F0.imprint","IMPRINT",FACE,{"disambiguationData":[TD([[makeQuery(id+"F0.imprint","IMPRINT",EDGE,{"derivedFrom":sQuery(id+"F0.wireOp",EDGE,"E0")}),1.0]])]});
            var Q1;
            Q1=makeQuery(id+"F0.imprint","IMPRINT",FACE,{"disambiguationData":[TD([[makeQuery(id+"F0.imprint","IMPRINT",EDGE,{"derivedFrom":sQuery(id+"F0.wireOp",EDGE,"E54")}),-1.0]])]});
            var Q2;
            Q2=makeQuery(id+"F0.imprint","IMPRINT",FACE,{"disambiguationData":[TD([[makeQuery(id+"F0.imprint","IMPRINT",EDGE,{"derivedFrom":sQuery(id+"F0.wireOp",EDGE,"E75")}),-1.0]])]});
            var Q3;
            Q3=makeQuery(id+"F0.imprint","IMPRINT",FACE,{"disambiguationData":[TD([[makeQuery(id+"F0.imprint","IMPRINT",EDGE,{"derivedFrom":sQuery(id+"F0.wireOp",EDGE,"E178")}),-1.0]])]});
            var Q4;
            Q4=makeQuery(id+"F0.imprint","IMPRINT",FACE,{"disambiguationData":[TD([[makeQuery(id+"F0.imprint","IMPRINT",EDGE,{"derivedFrom":sQuery(id+"F0.wireOp",EDGE,"E225")}),-1.0]])]});
            var Q5;
            Q5=makeQuery(id+"F0.imprint","IMPRINT",FACE,{"disambiguationData":[TD([[makeQuery(id+"F0.imprint","IMPRINT",EDGE,{"derivedFrom":sQuery(id+"F0.wireOp",EDGE,"E0")}),-1.0]])]});
            var Q6;
            Q6=makeQuery(id+"F0.imprint","IMPRINT",FACE,{"disambiguationData":[TD([[makeQuery(id+"F0.imprint","IMPRINT",EDGE,{"derivedFrom":sQuery(id+"F0.wireOp",EDGE,"E163")}),-1.0]])]});
            extrude(context, id + "F1", {"entities" : qUnion([Q0, Q1, Q2, Q3, Q4, Q5, Q6]), "oppositeDirection" : true, "depth" : 2 * mm, "offsetDistance" : 25 * mm});
        }
        {
            var Q0;
            Q0=makeQuery(id+"F0.imprint","IMPRINT",FACE,{"disambiguationData":[TD([[makeQuery(id+"F0.imprint","IMPRINT",EDGE,{"derivedFrom":sQuery(id+"F0.wireOp",EDGE,"E54")}),-1.0]])]});
            var Q1;
            Q1=makeQuery(id+"F0.imprint","IMPRINT",FACE,{"disambiguationData":[TD([[makeQuery(id+"F0.imprint","IMPRINT",EDGE,{"derivedFrom":sQuery(id+"F0.wireOp",EDGE,"E75")}),-1.0]])]});
            var Q2;
            Q2=makeQuery(id+"F0.imprint","IMPRINT",FACE,{"disambiguationData":[TD([[makeQuery(id+"F0.imprint","IMPRINT",EDGE,{"derivedFrom":sQuery(id+"F0.wireOp",EDGE,"E178")}),-1.0]])]});
            var Q3;
            Q3=makeQuery(id+"F0.imprint","IMPRINT",FACE,{"disambiguationData":[TD([[makeQuery(id+"F0.imprint","IMPRINT",EDGE,{"derivedFrom":sQuery(id+"F0.wireOp",EDGE,"E225")}),-1.0]])]});
            var Q4;
            Q4=makeQuery(id+"F0.imprint","IMPRINT",FACE,{"disambiguationData":[TD([[makeQuery(id+"F0.imprint","IMPRINT",EDGE,{"derivedFrom":sQuery(id+"F0.wireOp",EDGE,"E0")}),-1.0]])]});
            var Q5;
            Q5=makeQuery(id+"F0.imprint","IMPRINT",FACE,{"disambiguationData":[TD([[makeQuery(id+"F0.imprint","IMPRINT",EDGE,{"derivedFrom":sQuery(id+"F0.wireOp",EDGE,"E163")}),-1.0]])]});
            extrude(context, id + "F2", {"entities" : qUnion([Q0, Q1, Q2, Q3, Q4, Q5]), "operationType" : NewBodyOperationType.REMOVE, "oppositeDirection" : true, "depth" : 0.9 * mm, "offsetDistance" : 25 * mm});
        }
        {
            var Q0;
            Q0=makeQuery(id+"F1.opExtrude","CAP_EDGE",EDGE,{"disambiguationData":[OSD([sQuery(id+"F0.wireOp",EDGE,"E236")])],"isStart":true});
            fillet(context, id + "F3", {"entities" : qUnion([Q0]), "radius" : 0.5 * mm, "tangentPropagation" : true, "allowEdgeOverflow" : false});
        }
        {
            var Q0;
            Q0=makeQuery(id+"F1.opExtrude","CAP_FACE",FACE,{"disambiguationData":[OSD([sQuery(id+"F0.wireOp",EDGE,"E236")])],"isStart":false});
            var sketch = newSketch(context, id + "F4", { "sketchPlane" : qUnion([Q0])});
            skCircle(sketch, "E237", {"center": v(0, 0) * mm, "radius": 5.5 * mm});
            skCircle(sketch, "E238", {"center": v(0, 0) * mm, "radius": 4.1 * mm});
            skSolve(sketch);
        }
        {
            var Q0;
            Q0=makeQuery(id+"F4.imprint","IMPRINT",FACE,{"disambiguationData":[TD([[makeQuery(id+"F4.imprint","IMPRINT",EDGE,{"derivedFrom":sQuery(id+"F4.wireOp",EDGE,"E237")}),1.0]])]});
            extrude(context, id + "F5", {"entities" : qUnion([Q0]), "operationType" : NewBodyOperationType.ADD, "depth" : 1 * mm, "offsetDistance" : 25 * mm});
        }
        {
            var Q0;
            Q0=makeQuery(id+"F5.boolean.opBoolean","SPLIT",FACE,{"disambiguationData":[TD([makeQuery(id+"F5.opExtrude","SWEPT_FACE",FACE,{"disambiguationData":[OSD([sQuery(id+"F4.wireOp",EDGE,"E238")])]})])],"derivedFrom":makeQuery(id+"F1.opExtrude","CAP_FACE",FACE,{"disambiguationData":[OSD([sQuery(id+"F0.wireOp",EDGE,"E236")])],"isStart":false})});
            extrude(context, id + "F6", {"entities" : qUnion([Q0]), "operationType" : NewBodyOperationType.ADD, "depth" : 4.5 * mm, "offsetDistance" : 25 * mm});
        }
        {
            var Q0;
            Q0=makeQuery(id+"F6.opExtrude","CAP_EDGE",EDGE,{"disambiguationData":[OSD([sQuery(id+"F4.wireOp",EDGE,"E238")])],"isStart":false});
            fillet(context, id + "F7", {"entities" : qUnion([Q0]), "radius" : 0.5 * mm, "tangentPropagation" : true, "allowEdgeOverflow" : false});
        }
    });
